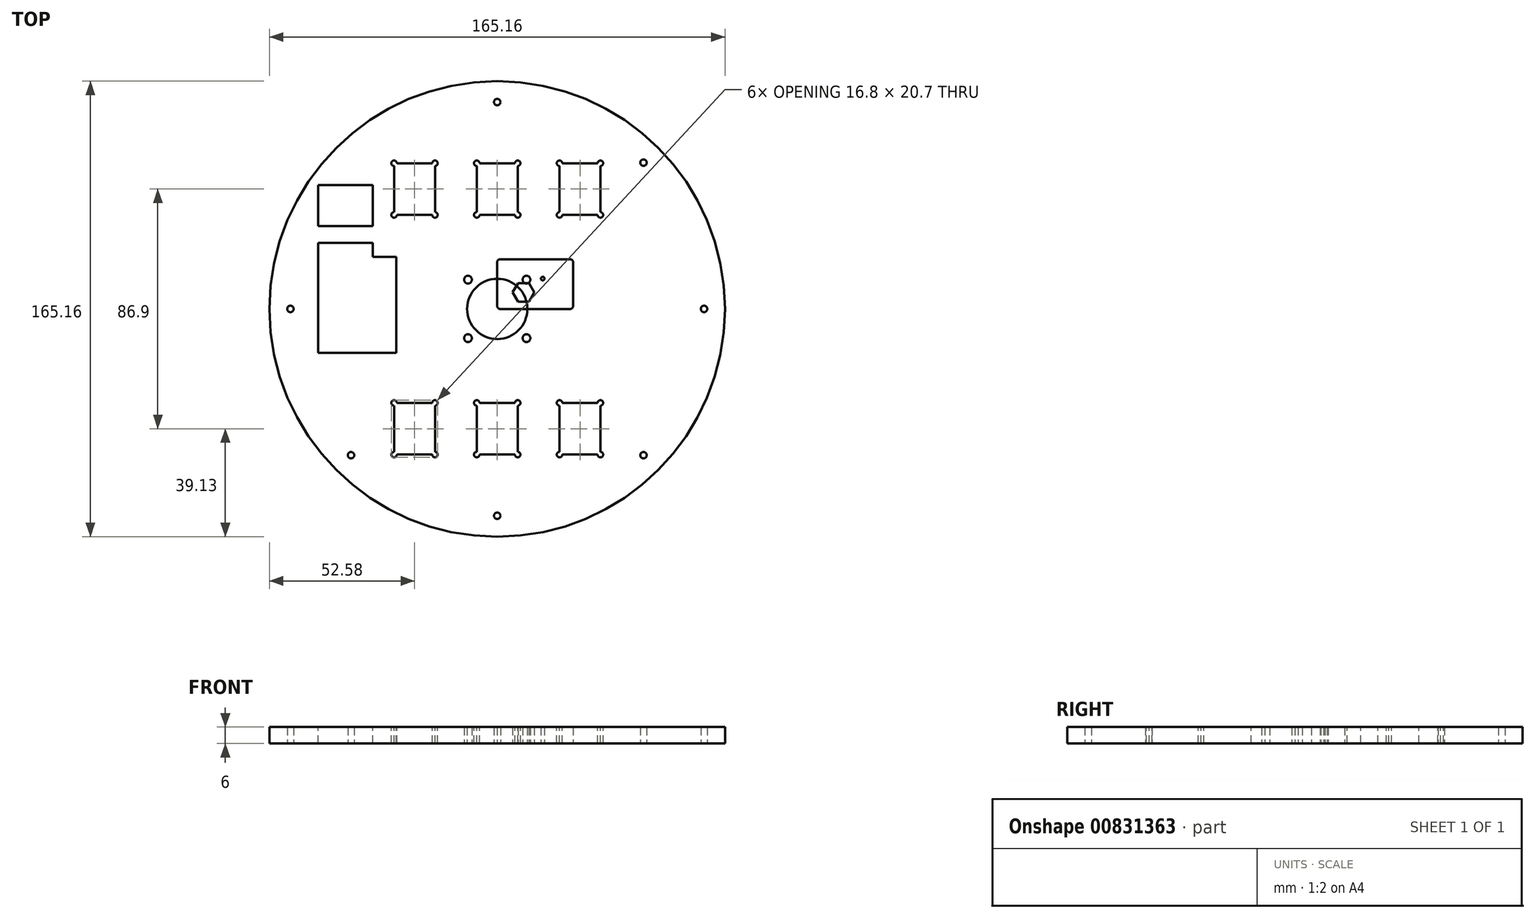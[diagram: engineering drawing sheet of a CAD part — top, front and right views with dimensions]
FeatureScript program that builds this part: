
annotation { "Feature Type Name" : "Feature", "Feature Type Description" : "" }
export const myFeature = defineFeature(function(context is Context, id is Id, definition is map)
    precondition{}
    {
        {
            var Q0;
            Q0=qCreatedBy(makeId("Top.planeOp"),FACE);
            var sketch = newSketch(context, id + "F0", { "sketchPlane" : qUnion([Q0])});
            skCircle(sketch, "E0", {"center": v(0, 0) * mm, "radius": 82.58 * mm});
            skCircle(sketch, "E1", {"center": v(0, 0) * mm, "radius": 75 * mm, "construction": true});
            skCircle(sketch, "E2", {"center": v(0, 75) * mm, "radius": 1.17 * mm});
            skCircle(sketch, "E3", {"center": v(53.03, 53.03) * mm, "radius": 1.17 * mm});
            skCircle(sketch, "E4", {"center": v(75, 0) * mm, "radius": 1.17 * mm});
            skCircle(sketch, "E5", {"center": v(53.03, -53.03) * mm, "radius": 1.17 * mm});
            skCircle(sketch, "E6", {"center": v(0, -75) * mm, "radius": 1.17 * mm});
            skCircle(sketch, "E7", {"center": v(-53.03, -53.03) * mm, "radius": 1.17 * mm});
            skCircle(sketch, "E8", {"center": v(-75, 0) * mm, "radius": 1.17 * mm});
            skLineSegment(sketch, "E9", {"start": v(0, 0) * mm, "end": v(53.03, 53.03) * mm, "construction": true});
            skLineSegment(sketch, "E10", {"start": v(0, 0) * mm, "end": v(53.03, -53.03) * mm, "construction": true});
            skLineSegment(sketch, "E11", {"start": v(0, 0) * mm, "end": v(-53.03, -53.03) * mm, "construction": true});
            skCircle(sketch, "E12", {"center": v(0, 0) * mm, "radius": 10.92 * mm});
            skCircle(sketch, "E13", {"center": v(0, 0) * mm, "radius": 15 * mm, "construction": true});
            skCircle(sketch, "E14", {"center": v(10.6, 10.6) * mm, "radius": 1.42 * mm});
            skCircle(sketch, "E15", {"center": v(-10.6, -10.6) * mm, "radius": 1.42 * mm});
            skCircle(sketch, "E16", {"center": v(10.6, -10.6) * mm, "radius": 1.42 * mm});
            skLineSegment(sketch, "E17", {"start": v(0, 0) * mm, "end": v(-53.03, 53.03) * mm, "construction": true});
            skCircle(sketch, "E18", {"center": v(-10.6, 10.6) * mm, "radius": 1.42 * mm});
            skSolve(sketch);
        }
        {
            var Q0;
            Q0 = qSketchRegion(id + "F0", true);
            extrude(context, id + "F1", {"entities" : qUnion([Q0]), "depth" : 6 * mm, "offsetDistance" : 25 * mm});
        }
        {
            var Q0;
            Q0=makeQuery(id+"F1.opExtrude","CAP_FACE",FACE,{"disambiguationData":[OSD([sQuery(id+"F0.wireOp",EDGE,"E0"),sQuery(id+"F0.wireOp",EDGE,"E2"),sQuery(id+"F0.wireOp",EDGE,"E3"),sQuery(id+"F0.wireOp",EDGE,"E4"),sQuery(id+"F0.wireOp",EDGE,"E5"),sQuery(id+"F0.wireOp",EDGE,"E6"),sQuery(id+"F0.wireOp",EDGE,"E7"),sQuery(id+"F0.wireOp",EDGE,"E8"),sQuery(id+"F0.wireOp",EDGE,"E12"),sQuery(id+"F0.wireOp",EDGE,"E14"),sQuery(id+"F0.wireOp",EDGE,"E15"),sQuery(id+"F0.wireOp",EDGE,"E16"),sQuery(id+"F0.wireOp",EDGE,"E18")])],"isStart":false});
            var sketch = newSketch(context, id + "F2", { "sketchPlane" : qUnion([Q0])});
            skLineSegment(sketch, "E19.bottom", {"start": v(-64.92, 44.92) * mm, "end": v(-45.08, 44.92) * mm});
            skLineSegment(sketch, "E19.top", {"start": v(-64.92, 30.08) * mm, "end": v(-45.08, 30.08) * mm});
            skLineSegment(sketch, "E19.left", {"start": v(-64.92, 44.92) * mm, "end": v(-64.92, 30.08) * mm});
            skLineSegment(sketch, "E19.right", {"start": v(-45.08, 44.92) * mm, "end": v(-45.08, 30.08) * mm});
            skLineSegment(sketch, "E20", {"start": v(-64.92, 23.92) * mm, "end": v(-64.92, -15.92) * mm});
            skLineSegment(sketch, "E21", {"start": v(-64.92, -15.92) * mm, "end": v(-36.58, -15.92) * mm});
            skLineSegment(sketch, "E22", {"start": v(-36.58, -15.92) * mm, "end": v(-36.58, 18.92) * mm});
            skLineSegment(sketch, "E23", {"start": v(-36.58, 18.92) * mm, "end": v(-45.08, 18.92) * mm});
            skLineSegment(sketch, "E24", {"start": v(-45.08, 18.92) * mm, "end": v(-45.08, 23.92) * mm});
            skLineSegment(sketch, "E25", {"start": v(-45.08, 23.92) * mm, "end": v(-64.92, 23.92) * mm});
            skSolve(sketch);
        }
        {
            var Q0;
            Q0 = qSketchRegion(id + "F2", true);
            extrude(context, id + "F3", {"entities" : qUnion([Q0]), "operationType" : NewBodyOperationType.REMOVE, "endBound" : BoundingType.THROUGH_ALL, "oppositeDirection" : true, "depth" : 25 * mm, "offsetDistance" : 25 * mm});
        }
        {
            var Q0;
            Q0=makeQuery(id+"F1.opExtrude","CAP_FACE",FACE,{"disambiguationData":[OSD([sQuery(id+"F0.wireOp",EDGE,"E0"),sQuery(id+"F0.wireOp",EDGE,"E2"),sQuery(id+"F0.wireOp",EDGE,"E3"),sQuery(id+"F0.wireOp",EDGE,"E4"),sQuery(id+"F0.wireOp",EDGE,"E5"),sQuery(id+"F0.wireOp",EDGE,"E6"),sQuery(id+"F0.wireOp",EDGE,"E7"),sQuery(id+"F0.wireOp",EDGE,"E8"),sQuery(id+"F0.wireOp",EDGE,"E12"),sQuery(id+"F0.wireOp",EDGE,"E14"),sQuery(id+"F0.wireOp",EDGE,"E15"),sQuery(id+"F0.wireOp",EDGE,"E16"),sQuery(id+"F0.wireOp",EDGE,"E18")])],"isStart":false});
            var sketch = newSketch(context, id + "F4", { "sketchPlane" : qUnion([Q0])});
            skLineSegment(sketch, "E26", {"start": v(-76.17, 0) * mm, "end": v(73.83, 0) * mm, "construction": true});
            skLineSegment(sketch, "E27.bottom", {"start": v(7.42, 34.08) * mm, "end": v(-7.42, 34.08) * mm});
            skLineSegment(sketch, "E27.top", {"start": v(7.42, 52.82) * mm, "end": v(-7.42, 52.82) * mm});
            skLineSegment(sketch, "E27.left", {"start": v(7.42, 34.08) * mm, "end": v(7.42, 52.82) * mm});
            skLineSegment(sketch, "E27.right", {"start": v(-7.42, 34.08) * mm, "end": v(-7.42, 52.82) * mm});
            skPoint(sketch, "E27.middle", {"position": v(0, 43.45) * mm});
            skLineSegment(sketch, "E28.bottom", {"start": v(37.42, 52.82) * mm, "end": v(22.58, 52.82) * mm});
            skLineSegment(sketch, "E28.top", {"start": v(37.42, 34.08) * mm, "end": v(22.58, 34.08) * mm});
            skLineSegment(sketch, "E28.left", {"start": v(37.42, 52.82) * mm, "end": v(37.42, 34.08) * mm});
            skLineSegment(sketch, "E28.right", {"start": v(22.58, 52.82) * mm, "end": v(22.58, 34.08) * mm});
            skPoint(sketch, "E28.middle", {"position": v(30, 43.45) * mm});
            skLineSegment(sketch, "E29.bottom", {"start": v(-22.58, 52.82) * mm, "end": v(-37.42, 52.82) * mm});
            skLineSegment(sketch, "E29.top", {"start": v(-22.58, 34.08) * mm, "end": v(-37.42, 34.08) * mm});
            skLineSegment(sketch, "E29.left", {"start": v(-22.58, 52.82) * mm, "end": v(-22.58, 34.08) * mm});
            skLineSegment(sketch, "E29.right", {"start": v(-37.42, 52.82) * mm, "end": v(-37.42, 34.08) * mm});
            skPoint(sketch, "E29.middle", {"position": v(-30, 43.45) * mm});
            skLineSegment(sketch, "E30.MirrorCS", {"start": v(37.42, -52.82) * mm, "end": v(37.42, -34.08) * mm});
            skLineSegment(sketch, "E31.MirrorCS", {"start": v(-22.58, -34.08) * mm, "end": v(-37.42, -34.08) * mm});
            skLineSegment(sketch, "E32.MirrorCS", {"start": v(-7.42, -34.08) * mm, "end": v(-7.42, -52.82) * mm});
            skPoint(sketch, "E33.MirrorP", {"position": v(-30, -43.45) * mm});
            skPoint(sketch, "E34.MirrorP", {"position": v(30, -43.45) * mm});
            skLineSegment(sketch, "E35.MirrorCS", {"start": v(7.42, -34.08) * mm, "end": v(-7.42, -34.08) * mm});
            skLineSegment(sketch, "E36.MirrorCS", {"start": v(-22.58, -52.82) * mm, "end": v(-37.42, -52.82) * mm});
            skLineSegment(sketch, "E37.MirrorCS", {"start": v(37.42, -34.08) * mm, "end": v(22.58, -34.08) * mm});
            skLineSegment(sketch, "E38.MirrorCS", {"start": v(-37.42, -52.82) * mm, "end": v(-37.42, -34.08) * mm});
            skLineSegment(sketch, "E39.MirrorCS", {"start": v(37.42, -52.82) * mm, "end": v(22.58, -52.82) * mm});
            skPoint(sketch, "E40.MirrorP", {"position": v(0, -43.45) * mm});
            skLineSegment(sketch, "E41.MirrorCS", {"start": v(7.42, -52.82) * mm, "end": v(-7.42, -52.82) * mm});
            skLineSegment(sketch, "E42.MirrorCS", {"start": v(7.42, -34.08) * mm, "end": v(7.42, -52.82) * mm});
            skLineSegment(sketch, "E43.MirrorCS", {"start": v(-22.58, -52.82) * mm, "end": v(-22.58, -34.08) * mm});
            skLineSegment(sketch, "E44.MirrorCS", {"start": v(22.58, -52.82) * mm, "end": v(22.58, -34.08) * mm});
            skSolve(sketch);
        }
        {
            var Q0;
            Q0=makeQuery(id+"F4.imprint","IMPRINT",FACE,{"disambiguationData":[TD([[makeQuery(id+"F4.imprint","IMPRINT",EDGE,{"derivedFrom":sQuery(id+"F4.wireOp",EDGE,"E27.bottom")}),1.0]])]});
            extrude(context, id + "F5", {"entities" : qUnion([Q0]), "operationType" : NewBodyOperationType.INTERSECT, "endBound" : BoundingType.THROUGH_ALL, "oppositeDirection" : true, "depth" : 25 * mm, "offsetDistance" : 25 * mm});
        }
        {
            var Q0;
            Q0=makeQuery(id+"F1.opExtrude","CAP_FACE",FACE,{"disambiguationData":[OSD([sQuery(id+"F0.wireOp",EDGE,"E0"),sQuery(id+"F0.wireOp",EDGE,"E2"),sQuery(id+"F0.wireOp",EDGE,"E3"),sQuery(id+"F0.wireOp",EDGE,"E4"),sQuery(id+"F0.wireOp",EDGE,"E5"),sQuery(id+"F0.wireOp",EDGE,"E6"),sQuery(id+"F0.wireOp",EDGE,"E7"),sQuery(id+"F0.wireOp",EDGE,"E8"),sQuery(id+"F0.wireOp",EDGE,"E12"),sQuery(id+"F0.wireOp",EDGE,"E14"),sQuery(id+"F0.wireOp",EDGE,"E15"),sQuery(id+"F0.wireOp",EDGE,"E16"),sQuery(id+"F0.wireOp",EDGE,"E18")])],"isStart":false});
            var sketch = newSketch(context, id + "F6", { "sketchPlane" : qUnion([Q0])});
            skCircle(sketch, "E45", {"center": v(-37.42, 52.82) * mm, "radius": 1 * mm});
            skCircle(sketch, "E46", {"center": v(-22.58, 52.82) * mm, "radius": 1 * mm});
            skCircle(sketch, "E47", {"center": v(-22.58, 34.08) * mm, "radius": 1 * mm});
            skCircle(sketch, "E48", {"center": v(-37.42, 34.08) * mm, "radius": 1 * mm});
            skCircle(sketch, "E49", {"center": v(-7.42, 34.08) * mm, "radius": 1 * mm});
            skCircle(sketch, "E50", {"center": v(-7.42, 52.82) * mm, "radius": 1 * mm});
            skCircle(sketch, "E51", {"center": v(7.42, 52.82) * mm, "radius": 1 * mm});
            skCircle(sketch, "E52", {"center": v(7.42, 34.08) * mm, "radius": 1 * mm});
            skCircle(sketch, "E53", {"center": v(22.58, 34.08) * mm, "radius": 1 * mm});
            skCircle(sketch, "E54", {"center": v(37.42, 34.08) * mm, "radius": 1 * mm});
            skCircle(sketch, "E55", {"center": v(37.42, 52.82) * mm, "radius": 1 * mm});
            skCircle(sketch, "E56", {"center": v(22.58, 52.82) * mm, "radius": 1 * mm});
            skCircle(sketch, "E57", {"center": v(37.42, -52.82) * mm, "radius": 1 * mm});
            skCircle(sketch, "E58", {"center": v(37.42, -34.08) * mm, "radius": 1 * mm});
            skCircle(sketch, "E59", {"center": v(22.58, -34.08) * mm, "radius": 1 * mm});
            skCircle(sketch, "E60", {"center": v(22.58, -52.82) * mm, "radius": 1 * mm});
            skCircle(sketch, "E61", {"center": v(7.42, -52.82) * mm, "radius": 1 * mm});
            skCircle(sketch, "E62", {"center": v(7.42, -34.08) * mm, "radius": 1 * mm});
            skCircle(sketch, "E63", {"center": v(-7.42, -34.08) * mm, "radius": 1 * mm});
            skCircle(sketch, "E64", {"center": v(-7.42, -52.82) * mm, "radius": 1 * mm});
            skCircle(sketch, "E65", {"center": v(-22.58, -52.82) * mm, "radius": 1 * mm});
            skCircle(sketch, "E66", {"center": v(-37.42, -52.82) * mm, "radius": 1 * mm});
            skCircle(sketch, "E67", {"center": v(-37.42, -34.08) * mm, "radius": 1 * mm});
            skCircle(sketch, "E68", {"center": v(-22.58, -34.08) * mm, "radius": 1 * mm});
            skSolve(sketch);
        }
        {
            var Q0;
            Q0 = qSketchRegion(id + "F6", true);
            extrude(context, id + "F7", {"entities" : qUnion([Q0]), "operationType" : NewBodyOperationType.REMOVE, "endBound" : BoundingType.THROUGH_ALL, "oppositeDirection" : true, "depth" : 25 * mm, "offsetDistance" : 25 * mm});
        }
        {
            var Q0;
            Q0=qCreatedBy(makeId("Top.planeOp"),FACE);
            var sketch = newSketch(context, id + "F8", { "sketchPlane" : qUnion([Q0])});
            skLineSegment(sketch, "E69.bottom", {"start": v(0, 0) * mm, "end": v(27.5, 0) * mm});
            skLineSegment(sketch, "E69.top", {"start": v(0, 18) * mm, "end": v(27.5, 18) * mm});
            skLineSegment(sketch, "E69.left", {"start": v(0, 0) * mm, "end": v(0, 18) * mm});
            skLineSegment(sketch, "E69.right", {"start": v(27.5, 0) * mm, "end": v(27.5, 18) * mm});
            skCircle(sketch, "E70", {"center": v(16.5, 11) * mm, "radius": 0.65 * mm});
            skCircle(sketch, "E71.cCircle", {"center": v(9.5, 6) * mm, "radius": 3.4 * mm, "construction": true});
            skLineSegment(sketch, "E71.0", {"start": v(13.43, 6) * mm, "end": v(11.46, 2.6) * mm});
            skLineSegment(sketch, "E71.1", {"start": v(11.46, 2.6) * mm, "end": v(7.54, 2.6) * mm});
            skLineSegment(sketch, "E71.2", {"start": v(7.54, 2.6) * mm, "end": v(5.57, 6) * mm});
            skLineSegment(sketch, "E71.3", {"start": v(5.57, 6) * mm, "end": v(7.54, 9.4) * mm});
            skLineSegment(sketch, "E71.4", {"start": v(7.54, 9.4) * mm, "end": v(11.46, 9.4) * mm});
            skLineSegment(sketch, "E71.5", {"start": v(11.46, 9.4) * mm, "end": v(13.43, 6) * mm});
            skPoint(sketch, "E71.0.midPoint", {"position": v(12.44, 4.3) * mm});
            skSolve(sketch);
        }
        {
            var Q0;
            Q0=makeQuery(id+"F8.imprint","IMPRINT",FACE,{"disambiguationData":[TD([[makeQuery(id+"F8.imprint","IMPRINT",EDGE,{"derivedFrom":sQuery(id+"F8.wireOp",EDGE,"E69.bottom")}),1.0]])]});
            extrude(context, id + "F9", {"entities" : qUnion([Q0]), "depth" : 6 * mm, "offsetDistance" : 25 * mm});
        }
        {
            var Q0;
            Q0=makeQuery(id+"F9.opExtrude","SWEPT_EDGE",EDGE,{"disambiguationData":[OSD([sQuery(id+"F8.wireOp",EDGE,"E69.top"),sQuery(id+"F8.wireOp",EDGE,"E69.left")])]});
            var Q1;
            Q1=makeQuery(id+"F9.opExtrude","SWEPT_EDGE",EDGE,{"disambiguationData":[OSD([sQuery(id+"F8.wireOp",EDGE,"E69.bottom"),sQuery(id+"F8.wireOp",EDGE,"E69.left")])]});
            var Q2;
            Q2=makeQuery(id+"F9.opExtrude","SWEPT_EDGE",EDGE,{"disambiguationData":[OSD([sQuery(id+"F8.wireOp",EDGE,"E69.bottom"),sQuery(id+"F8.wireOp",EDGE,"E69.right")])]});
            var Q3;
            Q3=makeQuery(id+"F9.opExtrude","SWEPT_EDGE",EDGE,{"disambiguationData":[OSD([sQuery(id+"F8.wireOp",EDGE,"E69.top"),sQuery(id+"F8.wireOp",EDGE,"E69.right")])]});
            fillet(context, id + "F10", {"entities" : qUnion([Q0, Q1, Q2, Q3]), "radius" : 1 * mm, "tangentPropagation" : true, "allowEdgeOverflow" : false});
        }
    });
